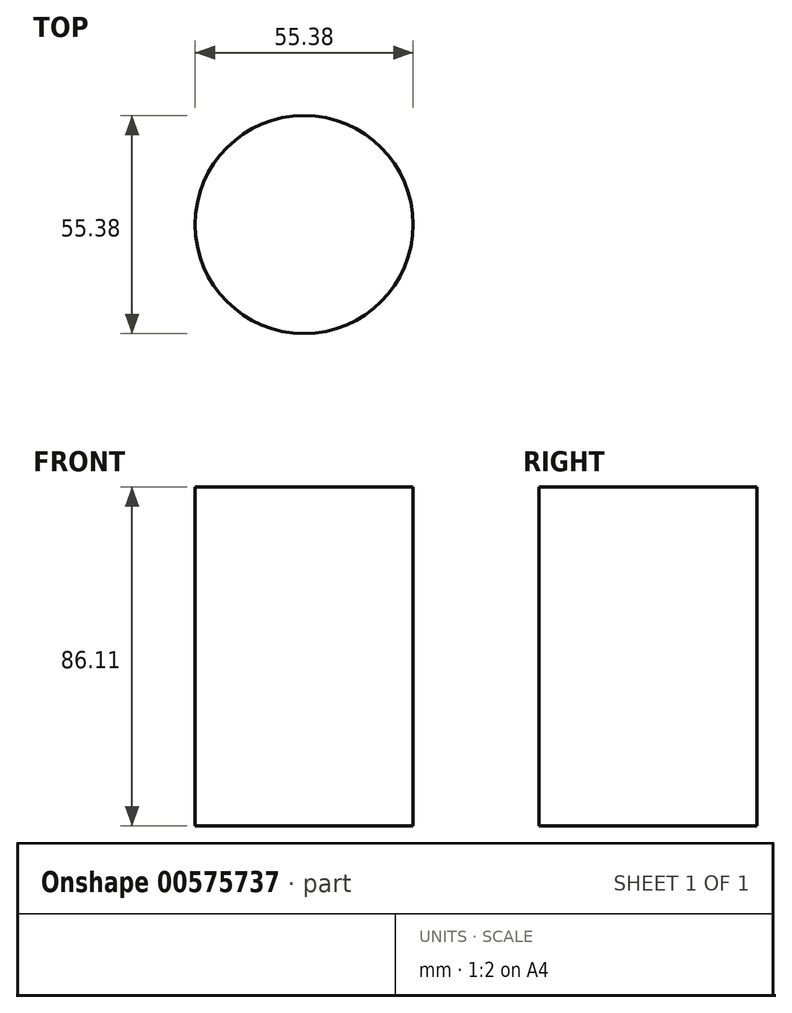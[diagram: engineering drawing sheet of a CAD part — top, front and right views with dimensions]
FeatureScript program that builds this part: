
annotation { "Feature Type Name" : "Feature", "Feature Type Description" : "" }
export const myFeature = defineFeature(function(context is Context, id is Id, definition is map)
    precondition{}
    {
        {
            var Q0;
            Q0=qCreatedBy(makeId("Top.planeOp"),FACE);
            var sketch = newSketch(context, id + "F0", { "sketchPlane" : qUnion([Q0])});
            skCircle(sketch, "E0", {"center": v(0, 0) * mm, "radius": 27.7 * mm});
            skSolve(sketch);
        }
        {
            var Q0;
            Q0 = qSketchRegion(id + "F0", true);
            extrude(context, id + "F1", {"entities" : qUnion([Q0]), "depth" : 86.1 * mm, "offsetDistance" : 25.4 * mm});
        }
    });
